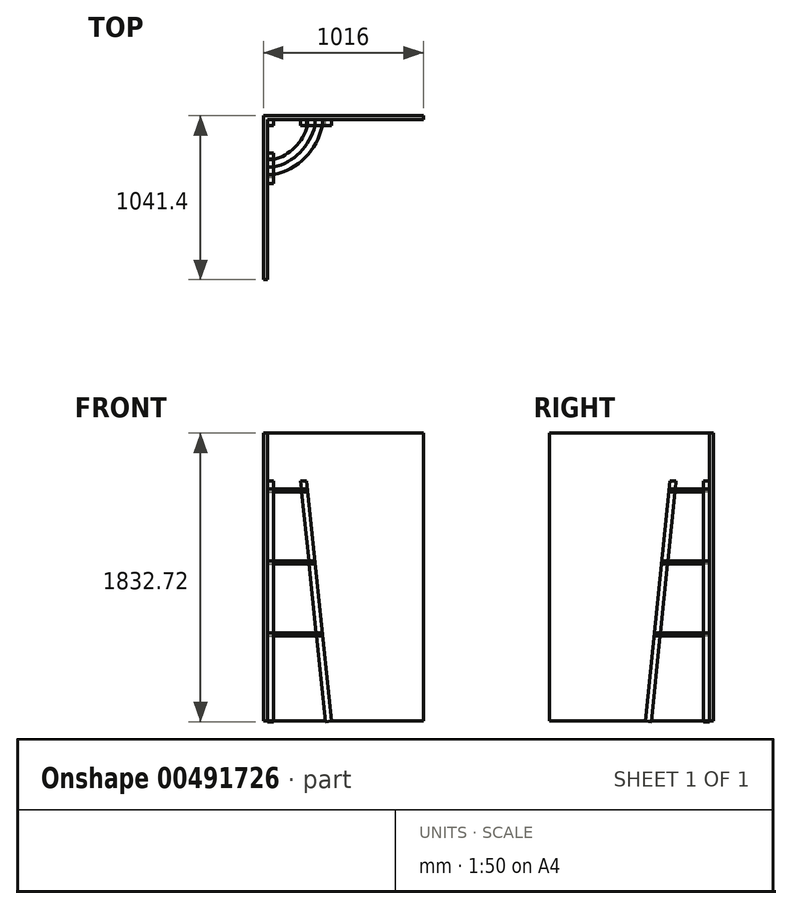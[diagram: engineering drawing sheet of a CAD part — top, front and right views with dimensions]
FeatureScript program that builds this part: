
annotation { "Feature Type Name" : "Feature", "Feature Type Description" : "" }
export const myFeature = defineFeature(function(context is Context, id is Id, definition is map)
    precondition{}
    {
        {
            var Q0;
            Q0=qCreatedBy(makeId("Top.planeOp"),FACE);
            var sketch = newSketch(context, id + "F0", { "sketchPlane" : qUnion([Q0])});
            skLineSegment(sketch, "E0.bottom", {"start": v(0, 0) * mm, "end": v(-25.4, 0) * mm});
            skLineSegment(sketch, "E0.top", {"start": v(0, -1016) * mm, "end": v(-25.4, -1016) * mm});
            skLineSegment(sketch, "E0.left", {"start": v(0, 0) * mm, "end": v(0, -1016) * mm});
            skLineSegment(sketch, "E0.right", {"start": v(-25.4, 0) * mm, "end": v(-25.4, -1016) * mm});
            skLineSegment(sketch, "E1.bottom", {"start": v(-25.4, 0) * mm, "end": v(990.6, 0) * mm});
            skLineSegment(sketch, "E1.top", {"start": v(-25.4, 25.4) * mm, "end": v(990.6, 25.4) * mm});
            skLineSegment(sketch, "E1.left", {"start": v(-25.4, 0) * mm, "end": v(-25.4, 25.4) * mm});
            skLineSegment(sketch, "E1.right", {"start": v(990.6, 0) * mm, "end": v(990.6, 25.4) * mm});
            skSolve(sketch);
        }
        {
            var Q0;
            Q0 = qSketchRegion(id + "F0", true);
            extrude(context, id + "F1", {"entities" : qUnion([Q0]), "depth" : 1828.8 * mm});
        }
        {
            var Q0;
            Q0=qCreatedBy(makeId("Top.planeOp"),FACE);
            var sketch = newSketch(context, id + "F2", { "sketchPlane" : qUnion([Q0])});
            skLineSegment(sketch, "E2.bottom", {"start": v(0, 0) * mm, "end": v(38.1, 0) * mm});
            skLineSegment(sketch, "E2.top", {"start": v(0, -38.1) * mm, "end": v(38.1, -38.1) * mm});
            skLineSegment(sketch, "E2.left", {"start": v(0, 0) * mm, "end": v(0, -38.1) * mm});
            skLineSegment(sketch, "E2.right", {"start": v(38.1, 0) * mm, "end": v(38.1, -38.1) * mm});
            skSolve(sketch);
        }
        {
            var Q0;
            Q0 = qSketchRegion(id + "F2", true);
            extrude(context, id + "F3", {"entities" : qUnion([Q0]), "depth" : 1524 * mm});
        }
        {
            var Q0;
            Q0=makeQuery(id+"F3.opExtrude","SWEPT_FACE",FACE,{"disambiguationData":[OSD([sQuery(id+"F2.wireOp",EDGE,"E2.left")])]});
            var sketch = newSketch(context, id + "F4", { "sketchPlane" : qUnion([Q0])});
            skLineSegment(sketch, "E3", {"start": v(254, 1473.2) * mm, "end": v(406.4, 0) * mm});
            skSolve(sketch);
        }
        {
            var Q0;
            Q0=makeQuery(id+"F3.opExtrude","CAP_FACE",FACE,{"disambiguationData":[OSD([sQuery(id+"F2.wireOp",EDGE,"E2.bottom"),sQuery(id+"F2.wireOp",EDGE,"E2.top"),sQuery(id+"F2.wireOp",EDGE,"E2.left"),sQuery(id+"F2.wireOp",EDGE,"E2.right")])],"isStart":false});
            var Q1;
            Q1=sQuery(id+"F4.wireOp",VERTEX,"E3.start");
            cPlane(context, id + "F5", {"entities" : qUnion([Q0, Q1]), "cplaneType" : CPlaneType.PLANE_POINT, "offset" : 25.4 * mm, "width" : 152.4 * mm, "height" : 152.4 * mm});
        }
        {
            var Q0;
            Q0=qCreatedBy(id+"F5.planeOp",FACE);
            var sketch = newSketch(context, id + "F6", { "sketchPlane" : qUnion([Q0])});
            skLineSegment(sketch, "E4.bottom", {"start": v(0, 0) * mm, "end": v(254, 0) * mm});
            skLineSegment(sketch, "E4.top", {"start": v(0, -254) * mm, "end": v(254, -254) * mm});
            skLineSegment(sketch, "E4.left", {"start": v(0, 0) * mm, "end": v(0, -254) * mm});
            skLineSegment(sketch, "E4.right", {"start": v(254, 0) * mm, "end": v(254, -254) * mm});
            skSolve(sketch);
        }
        {
            var Q0;
            Q0 = qSketchRegion(id + "F6", true);
            extrude(context, id + "F7", {"entities" : qUnion([Q0]), "oppositeDirection" : true, "depth" : 19.05 * mm});
        }
        {
            var Q0;
            Q0=qCreatedBy(id+"F5.planeOp",FACE);
            cPlane(context, id + "F8", {"entities" : qUnion([Q0]), "cplaneType" : CPlaneType.OFFSET, "offset" : 457.2 * mm, "oppositeDirection" : true, "width" : 152.4 * mm, "height" : 152.4 * mm});
        }
        {
            var Q0;
            Q0=qCreatedBy(id+"F8.planeOp",FACE);
            var sketch = newSketch(context, id + "F9", { "sketchPlane" : qUnion([Q0])});
            skLineSegment(sketch, "E5.bottom", {"start": v(0, 0) * mm, "end": v(301.3, 0) * mm});
            skLineSegment(sketch, "E5.top", {"start": v(0, -301.3) * mm, "end": v(301.3, -301.3) * mm});
            skLineSegment(sketch, "E5.left", {"start": v(0, 0) * mm, "end": v(0, -301.3) * mm});
            skLineSegment(sketch, "E5.right", {"start": v(301.3, 0) * mm, "end": v(301.3, -301.3) * mm});
            skSolve(sketch);
        }
        {
            var Q0;
            Q0 = qSketchRegion(id + "F9", true);
            extrude(context, id + "F10", {"entities" : qUnion([Q0]), "oppositeDirection" : true, "depth" : 19.05 * mm});
        }
        {
            var Q0;
            Q0=sQuery(id+"F4.wireOp",EDGE,"E3");
            var Q1;
            Q1=sQuery(id+"F4.wireOp",VERTEX,"E3.end");
            cPlane(context, id + "F11", {"entities" : qUnion([Q0, Q1]), "cplaneType" : CPlaneType.CURVE_POINT, "offset" : 25.4 * mm, "width" : 152.4 * mm, "height" : 152.4 * mm});
        }
        {
            var Q0;
            Q0=qCreatedBy(id+"F11.planeOp",FACE);
            var sketch = newSketch(context, id + "F12", { "sketchPlane" : qUnion([Q0])});
            skLineSegment(sketch, "E6.bottom", {"start": v(38.1, 366.14) * mm, "end": v(0, 366.14) * mm});
            skLineSegment(sketch, "E6.top", {"start": v(38.1, 404.24) * mm, "end": v(0, 404.24) * mm});
            skLineSegment(sketch, "E6.left", {"start": v(38.1, 366.14) * mm, "end": v(38.1, 404.24) * mm});
            skLineSegment(sketch, "E6.right", {"start": v(0, 366.14) * mm, "end": v(0, 404.24) * mm});
            skSolve(sketch);
        }
        {
            var Q0;
            Q0 = qSketchRegion(id + "F12", true);
            var Q1;
            Q1=makeQuery(id+"F3.opExtrude","CAP_FACE",FACE,{"disambiguationData":[OSD([sQuery(id+"F2.wireOp",EDGE,"E2.bottom"),sQuery(id+"F2.wireOp",EDGE,"E2.top"),sQuery(id+"F2.wireOp",EDGE,"E2.left"),sQuery(id+"F2.wireOp",EDGE,"E2.right")])],"isStart":false});
            var Q2;
            Q2=makeQuery(id+"F3.opExtrude","CAP_FACE",FACE,{"disambiguationData":[OSD([sQuery(id+"F2.wireOp",EDGE,"E2.bottom"),sQuery(id+"F2.wireOp",EDGE,"E2.top"),sQuery(id+"F2.wireOp",EDGE,"E2.left"),sQuery(id+"F2.wireOp",EDGE,"E2.right")])],"isStart":true});
            extrude(context, id + "F13", {"entities" : qUnion([Q0]), "endBound" : BoundingType.UP_TO_SURFACE, "oppositeDirection" : true, "endBoundEntityFace" : qUnion([Q1]), "depth" : 25.4 * mm});
        }
        {
            var Q0;
            Q0=makeQuery(id+"F7.opExtrude","CAP_VERTEX",VERTEX,{"disambiguationData":[OSD([sQuery(id+"F6.wireOp",EDGE,"E4.bottom"),sQuery(id+"F6.wireOp",EDGE,"E4.left")])],"isStart":true});
            var Q1;
            Q1=makeQuery(id+"F7.opExtrude","CAP_VERTEX",VERTEX,{"disambiguationData":[OSD([sQuery(id+"F6.wireOp",EDGE,"E4.top"),sQuery(id+"F6.wireOp",EDGE,"E4.right")])],"isStart":true});
            var Q2;
            Q2=makeQuery(id+"F7.opExtrude","CAP_VERTEX",VERTEX,{"disambiguationData":[OSD([sQuery(id+"F6.wireOp",EDGE,"E4.top"),sQuery(id+"F6.wireOp",EDGE,"E4.right")])],"isStart":false});
            cPlane(context, id + "F14", {"entities" : qUnion([Q0, Q1, Q2]), "cplaneType" : CPlaneType.THREE_POINT, "offset" : 25.4 * mm, "width" : 152.4 * mm, "height" : 152.4 * mm});
        }
        {
            var Q0;
            Q0=makeQuery(id+"F13.opExtrude","SWEPT_BODY",BODY,{"disambiguationData":[OSD([sQuery(id+"F12.wireOp",EDGE,"E6.bottom"),sQuery(id+"F12.wireOp",EDGE,"E6.top"),sQuery(id+"F12.wireOp",EDGE,"E6.left"),sQuery(id+"F12.wireOp",EDGE,"E6.right")])]});
            var Q1;
            Q1=qCreatedBy(id+"F14.planeOp",FACE);
            mirror(context, id + "F15", {"entities" : qUnion([Q0]), "mirrorPlane" : qUnion([Q1])});
        }
        {
            var Q0;
            Q0=makeQuery(id+"F7.opExtrude","CAP_FACE",FACE,{"disambiguationData":[OSD([sQuery(id+"F6.wireOp",EDGE,"E4.bottom"),sQuery(id+"F6.wireOp",EDGE,"E4.top"),sQuery(id+"F6.wireOp",EDGE,"E4.left"),sQuery(id+"F6.wireOp",EDGE,"E4.right")])],"isStart":true});
            var sketch = newSketch(context, id + "F16", { "sketchPlane" : qUnion([Q0])});
            skArc(sketch, "E7", {"start": v(38.1, -254) * mm, "mid": v(175.03, -175.03) * mm, "end": v(254, -38.1) * mm});
            skLineSegment(sketch, "E8", {"start": v(38.1, -254) * mm, "end": v(254, -254) * mm});
            skLineSegment(sketch, "E9", {"start": v(254, -254) * mm, "end": v(254, -38.1) * mm});
            skSolve(sketch);
        }
        {
            var Q0;
            Q0 = qSketchRegion(id + "F16", true);
            extrude(context, id + "F17", {"entities" : qUnion([Q0]), "operationType" : NewBodyOperationType.REMOVE, "oppositeDirection" : true, "depth" : 25.4 * mm});
        }
        {
            var Q0;
            Q0=makeQuery(id+"F10.opExtrude","CAP_FACE",FACE,{"disambiguationData":[OSD([sQuery(id+"F9.wireOp",EDGE,"E5.bottom"),sQuery(id+"F9.wireOp",EDGE,"E5.top"),sQuery(id+"F9.wireOp",EDGE,"E5.left"),sQuery(id+"F9.wireOp",EDGE,"E5.right")])],"isStart":true});
            var sketch = newSketch(context, id + "F18", { "sketchPlane" : qUnion([Q0])});
            skArc(sketch, "E10", {"start": v(38.1, -301.3) * mm, "mid": v(207.5, -207.5) * mm, "end": v(301.3, -38.1) * mm});
            skLineSegment(sketch, "E11", {"start": v(38.1, -301.3) * mm, "end": v(301.3, -301.3) * mm});
            skLineSegment(sketch, "E12", {"start": v(301.3, -301.3) * mm, "end": v(301.3, -38.1) * mm});
            skSolve(sketch);
        }
        {
            var Q0;
            Q0 = qSketchRegion(id + "F18", true);
            extrude(context, id + "F19", {"entities" : qUnion([Q0]), "operationType" : NewBodyOperationType.REMOVE, "oppositeDirection" : true, "depth" : 25.4 * mm});
        }
        {
            var Q0;
            Q0=qCreatedBy(id+"F8.planeOp",FACE);
            cPlane(context, id + "F20", {"entities" : qUnion([Q0]), "cplaneType" : CPlaneType.OFFSET, "offset" : 457.2 * mm, "oppositeDirection" : true, "width" : 152.4 * mm, "height" : 152.4 * mm});
        }
        {
            var Q0;
            Q0=qCreatedBy(id+"F20.planeOp",FACE);
            var sketch = newSketch(context, id + "F21", { "sketchPlane" : qUnion([Q0])});
            skLineSegment(sketch, "E13.bottom", {"start": v(0, 0) * mm, "end": v(348.6, 0) * mm});
            skLineSegment(sketch, "E13.top", {"start": v(0, -348.6) * mm, "end": v(348.6, -348.6) * mm});
            skLineSegment(sketch, "E13.left", {"start": v(0, 0) * mm, "end": v(0, -348.6) * mm});
            skLineSegment(sketch, "E13.right", {"start": v(348.6, 0) * mm, "end": v(348.6, -348.6) * mm});
            skArc(sketch, "E14", {"start": v(38.1, -348.6) * mm, "mid": v(240.19, -240.19) * mm, "end": v(348.6, -38.1) * mm});
            skSolve(sketch);
        }
        {
            var Q0;
            {var subQ1=sQuery(id+"F21.wireOp",EDGE,"E13.bottom");Q0=makeQuery(id+"F21.imprint","IMPRINT",FACE,{"disambiguationData":[TD([[makeQuery(id+"F21.imprint","IMPRINT",EDGE,{"derivedFrom":subQ1}),-1.0]])]});}
            extrude(context, id + "F22", {"entities" : qUnion([Q0]), "oppositeDirection" : true, "depth" : 19.05 * mm});
        }
    });
